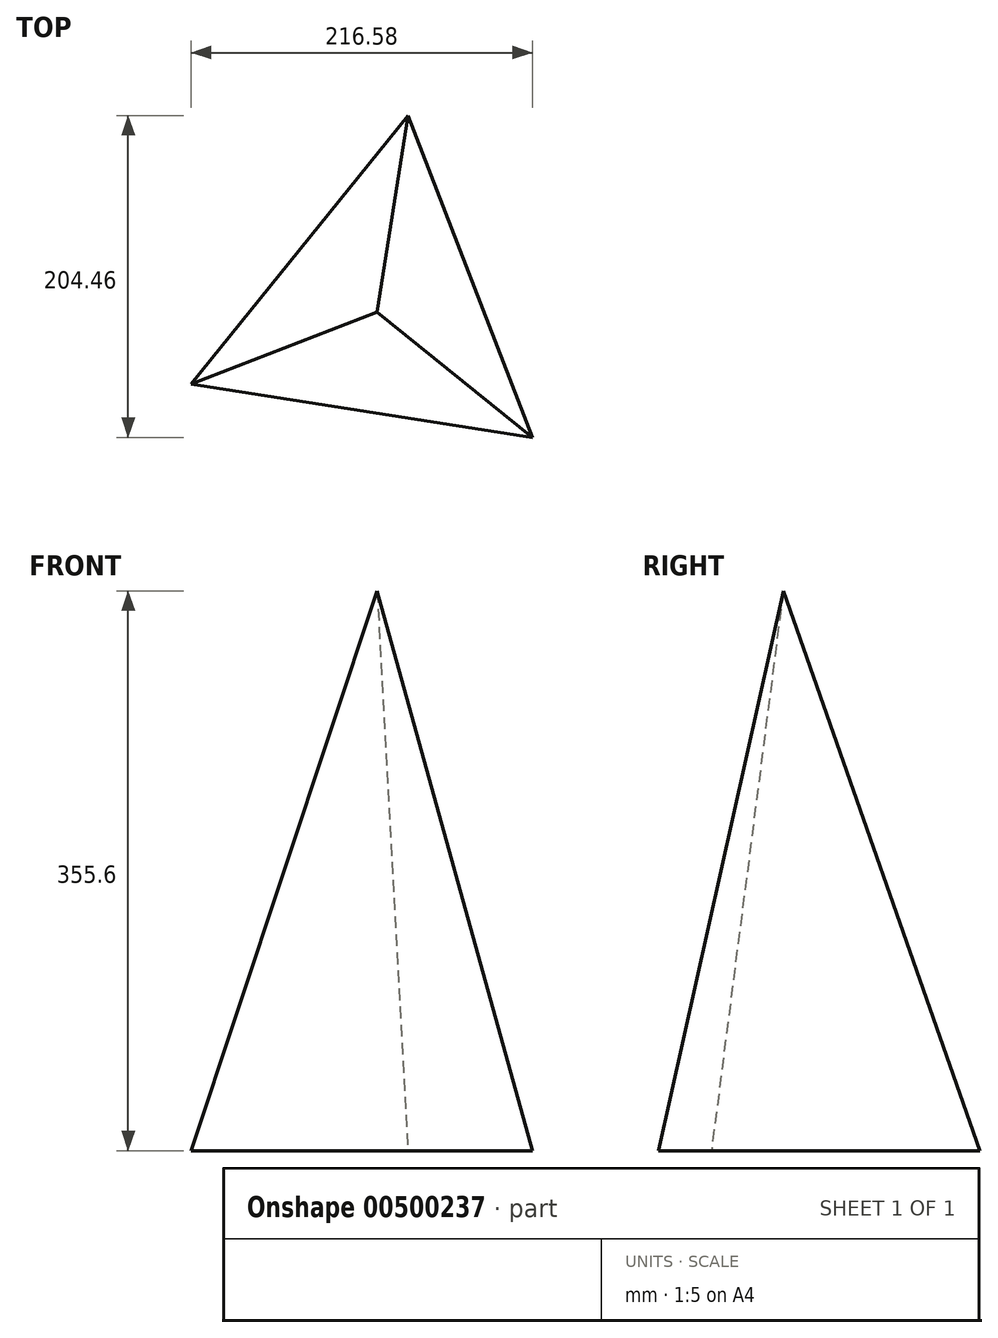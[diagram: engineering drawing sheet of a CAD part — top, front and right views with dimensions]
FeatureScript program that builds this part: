
annotation { "Feature Type Name" : "Feature", "Feature Type Description" : "" }
export const myFeature = defineFeature(function(context is Context, id is Id, definition is map)
    precondition{}
    {
        {
            var Q0;
            Q0=qCreatedBy(makeId("Top.planeOp"),FACE);
            var sketch = newSketch(context, id + "F0", { "sketchPlane" : qUnion([Q0])});
            skCircle(sketch, "E0.cCircle", {"center": v(0, 0) * mm, "radius": 126.55 * mm, "construction": true});
            skLineSegment(sketch, "E0.0", {"start": v(-118.05, -45.62) * mm, "end": v(19.52, 125.04) * mm});
            skLineSegment(sketch, "E0.1", {"start": v(19.52, 125.04) * mm, "end": v(98.53, -79.42) * mm});
            skLineSegment(sketch, "E0.2", {"start": v(98.53, -79.42) * mm, "end": v(-118.05, -45.62) * mm});
            skSolve(sketch);
        }
        {
            var Q0;
            Q0=qCreatedBy(makeId("Top.planeOp"),FACE);
            cPlane(context, id + "F1", {"entities" : qUnion([Q0]), "cplaneType" : CPlaneType.OFFSET, "offset" : 355.6 * mm, "width" : 152.4 * mm, "height" : 152.4 * mm});
        }
        {
            var Q0;
            Q0=qCreatedBy(id+"F1.planeOp",FACE);
            var sketch = newSketch(context, id + "F2", { "sketchPlane" : qUnion([Q0])});
            skPoint(sketch, "E1", {"position": v(0, 0) * mm});
            skSolve(sketch);
        }
        {
            var Q0;
            Q0=sQuery(id+"F2.wireOp",VERTEX,"E1");
            var Q1;
            Q1=makeQuery(id+"F0.imprint","IMPRINT",FACE,{"disambiguationData":[TD([[makeQuery(id+"F0.imprint","IMPRINT",EDGE,{"derivedFrom":sQuery(id+"F0.wireOp",EDGE,"E0.0")}),-1.0]])]});
            loft(context, id + "F3", {"sheetProfilesArray" : [{ "sheetProfileEntities" : qUnion([Q0]) }, { "sheetProfileEntities" : qUnion([Q1]) }]});
        }
    });
